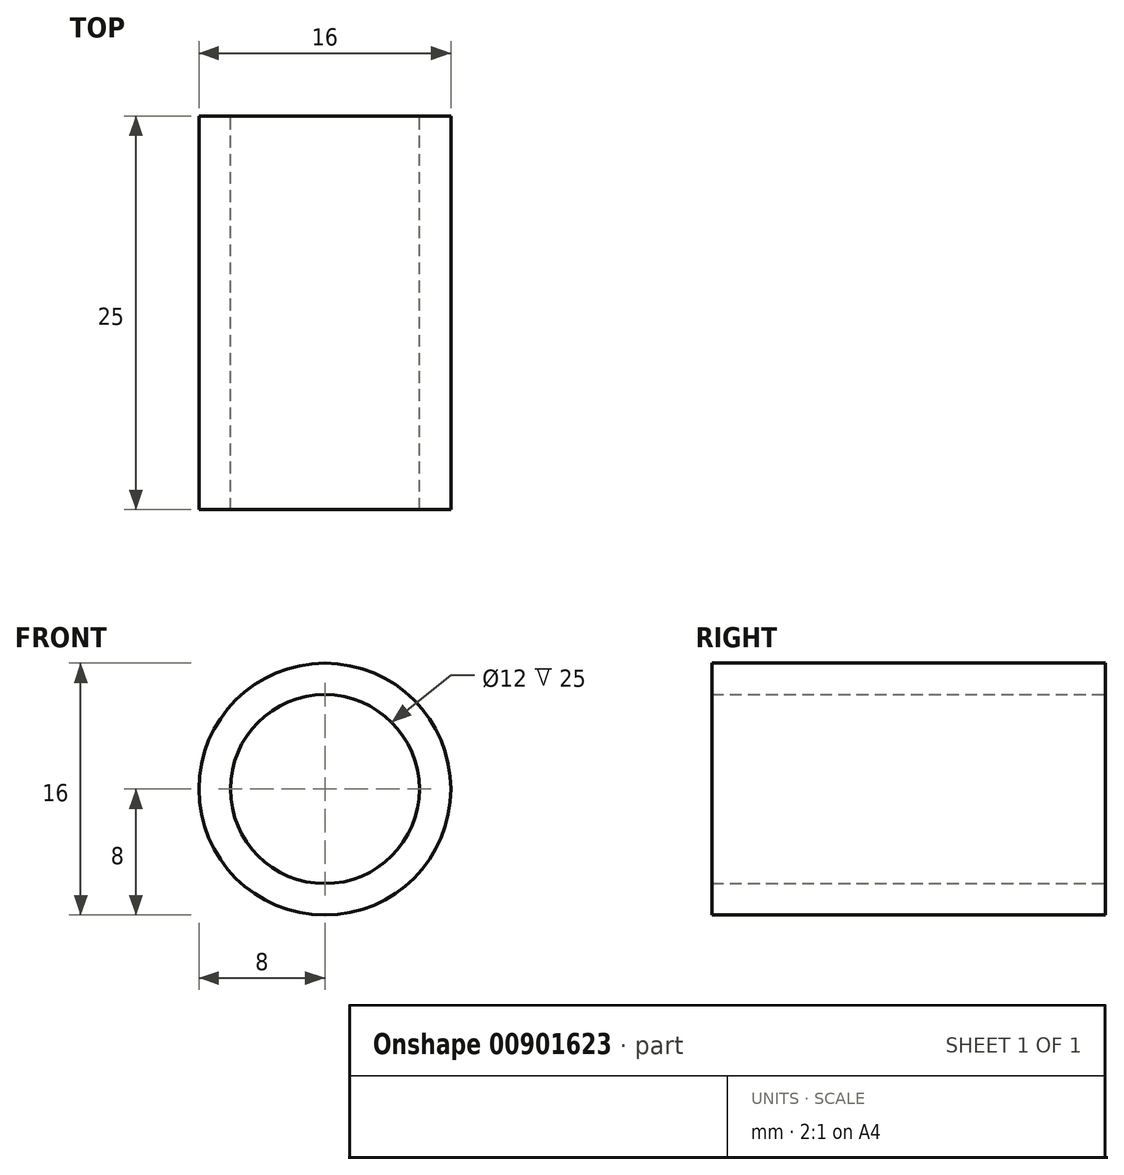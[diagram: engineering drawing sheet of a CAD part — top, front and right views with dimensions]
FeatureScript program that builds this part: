
annotation { "Feature Type Name" : "Feature", "Feature Type Description" : "" }
export const myFeature = defineFeature(function(context is Context, id is Id, definition is map)
    precondition{}
    {
        {
            var Q0;
            Q0=qCreatedBy(makeId("Front.planeOp"),FACE);
            var sketch = newSketch(context, id + "F0", { "sketchPlane" : qUnion([Q0])});
            skCircle(sketch, "E0", {"center": v(0, 0) * mm, "radius": 6 * mm});
            skCircle(sketch, "E1", {"center": v(0, 0) * mm, "radius": 8 * mm});
            skSolve(sketch);
        }
        {
            var Q0;
            Q0=makeQuery(id+"F0.imprint","IMPRINT",FACE,{"disambiguationData":[TD([[makeQuery(id+"F0.imprint","IMPRINT",EDGE,{"derivedFrom":sQuery(id+"F0.wireOp",EDGE,"E0")}),-1.0]])]});
            extrude(context, id + "F1", {"entities" : qUnion([Q0]), "depth" : 25 * mm, "offsetDistance" : 25 * mm});
        }
    });
